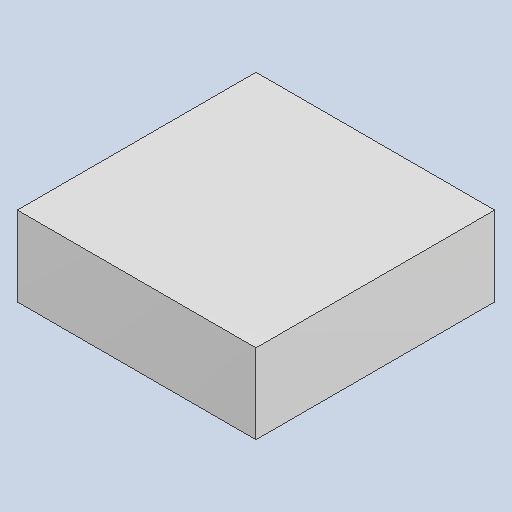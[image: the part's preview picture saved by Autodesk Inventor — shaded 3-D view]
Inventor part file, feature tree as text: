
AUTODESK INVENTOR PART (.ipt)
format: ipt  version: 2023.4 (Build 274418000, 418)  size: 79,872 bytes
history: native  units: mm
features: extrude x1
ambient origin geometry x8: Origin, YZ Plane, XZ Plane, XY Plane, X Axis, Y Axis, Z Axis, Center Point
bodies: Solid1 (feature_tree)
feature tree (1):
  extrude  "Extruded_32"  [1 undecoded]
note: 1 required parameter value undecoded (feature->parameter linkage not recoverable at this tier; creation-order binding heuristic only, values carry confidence <= 0.55)
